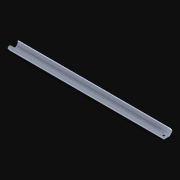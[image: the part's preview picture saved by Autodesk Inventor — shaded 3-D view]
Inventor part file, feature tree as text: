
AUTODESK INVENTOR PART (.ipt)
format: ipt  version: 2021 (Build 250183000, 183)  size: 443,392 bytes
history: native  units: in
note: dims shown in document units (in); Inventor stores cm internally (conversion verified against a paired STEP export)
features: other x25, extrude x24, imported_body x1, pattern_linear x1
ambient origin geometry x8: Origin, YZ Plane, XZ Plane, XY Plane, X Axis, Y Axis, Z Axis, Center Point
bodies: Body1 (feature_tree), Body2 (feature_tree), Body3 (feature_tree), Body4 (feature_tree), Body5 (feature_tree), Body6 (feature_tree), Body7 (feature_tree), Body8 (feature_tree), Body9 (feature_tree), Body10 (feature_tree), Body11 (feature_tree), Body12 (feature_tree), Body13 (feature_tree), Body14 (feature_tree), Body15 (feature_tree), Body16 (feature_tree), Body17 (feature_tree), Body18 (feature_tree), Body19 (feature_tree), Body20 (feature_tree), Body21 (feature_tree), Body22 (feature_tree), Body23 (feature_tree), Body24 (feature_tree), Body25 (feature_tree)
feature tree (51):
  parser-record x1  (decoder bookkeeping rows leaked as tree rows — omitted from the tree; the rows remain in map.json)
  imported_body  "Base1"
  pattern_linear  "Rectangular Pattern1"  Spacing1=0.046in  [1 undecoded]
  other  "Srf1"
  other  "Srf2"
  other  "Srf3"
  other  "Srf4"
  other  "Srf5"
  other  "Srf6"
  other  "Srf7"
  other  "Srf8"
  other  "Srf9"
  other  "Srf10"
  other  "Srf11"
  other  "Srf12"
  other  "Srf13"
  other  "Srf14"
  other  "Srf15"
  other  "Srf16"
  other  "Srf17"
  other  "Srf18"
  other  "Srf19"
  other  "Srf20"
  other  "Srf21"
  other  "Srf22"
  other  "Srf23"
  other  "Srf24"
  extrude  "ExtrusionSrf1"  Depth=0.5in
  extrude  "ExtrusionSrf2"  [1 undecoded]
  extrude  "ExtrusionSrf3"  [1 undecoded]
  extrude  "ExtrusionSrf4"  [1 undecoded]
  extrude  "ExtrusionSrf5"  [1 undecoded]
  extrude  "ExtrusionSrf6"  [1 undecoded]
  extrude  "ExtrusionSrf7"  [1 undecoded]
  extrude  "ExtrusionSrf8"  [1 undecoded]
  extrude  "ExtrusionSrf9"  [1 undecoded]
  extrude  "ExtrusionSrf10"  [1 undecoded]
  extrude  "ExtrusionSrf11"  [1 undecoded]
  extrude  "ExtrusionSrf12"  [1 undecoded]
  extrude  "ExtrusionSrf13"  [1 undecoded]
  extrude  "ExtrusionSrf14"  [1 undecoded]
  extrude  "ExtrusionSrf15"  [1 undecoded]
  extrude  "ExtrusionSrf16"  [1 undecoded]
  extrude  "ExtrusionSrf17"  [1 undecoded]
  extrude  "ExtrusionSrf18"  [1 undecoded]
  extrude  "ExtrusionSrf19"  [1 undecoded]
  extrude  "ExtrusionSrf20"  [1 undecoded]
  extrude  "ExtrusionSrf21"  [1 undecoded]
  extrude  "ExtrusionSrf22"  [1 undecoded]
  extrude  "ExtrusionSrf23"  [1 undecoded]
  extrude  "ExtrusionSrf24"  [1 undecoded]
note: 24 required parameter values undecoded (feature->parameter linkage not recoverable at this tier; creation-order binding heuristic only, values carry confidence <= 0.55)
